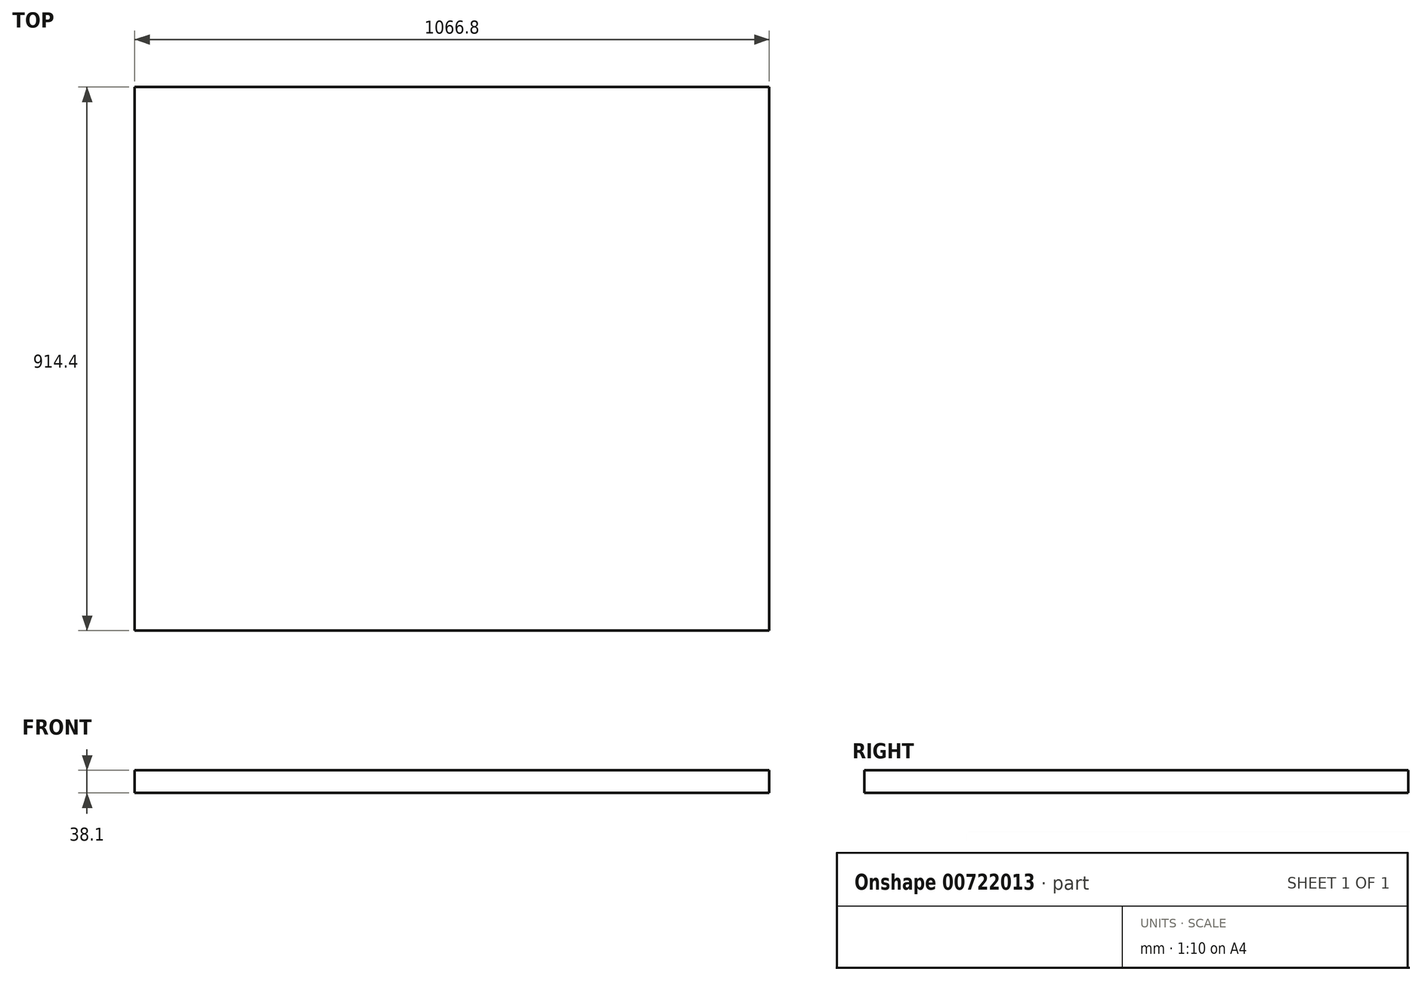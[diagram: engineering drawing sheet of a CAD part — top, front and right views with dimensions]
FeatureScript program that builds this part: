
annotation { "Feature Type Name" : "Feature", "Feature Type Description" : "" }
export const myFeature = defineFeature(function(context is Context, id is Id, definition is map)
    precondition{}
    {
        {
            var Q0;
            Q0=qCreatedBy(makeId("Top.planeOp"),FACE);
            var sketch = newSketch(context, id + "F0", { "sketchPlane" : qUnion([Q0])});
            skLineSegment(sketch, "E0.bottom", {"start": v(-452.63, 376.57) * mm, "end": v(614.17, 376.57) * mm});
            skLineSegment(sketch, "E0.top", {"start": v(-452.63, -537.83) * mm, "end": v(614.17, -537.83) * mm});
            skLineSegment(sketch, "E0.left", {"start": v(-452.63, 376.57) * mm, "end": v(-452.63, -537.83) * mm});
            skLineSegment(sketch, "E0.right", {"start": v(614.17, 376.57) * mm, "end": v(614.17, -537.83) * mm});
            skSolve(sketch);
        }
        {
            var Q0;
            Q0 = qSketchRegion(id + "F0", true);
            extrude(context, id + "F1", {"entities" : qUnion([Q0]), "depth" : 38.1 * mm, "offsetDistance" : 25.4 * mm});
        }
    });
